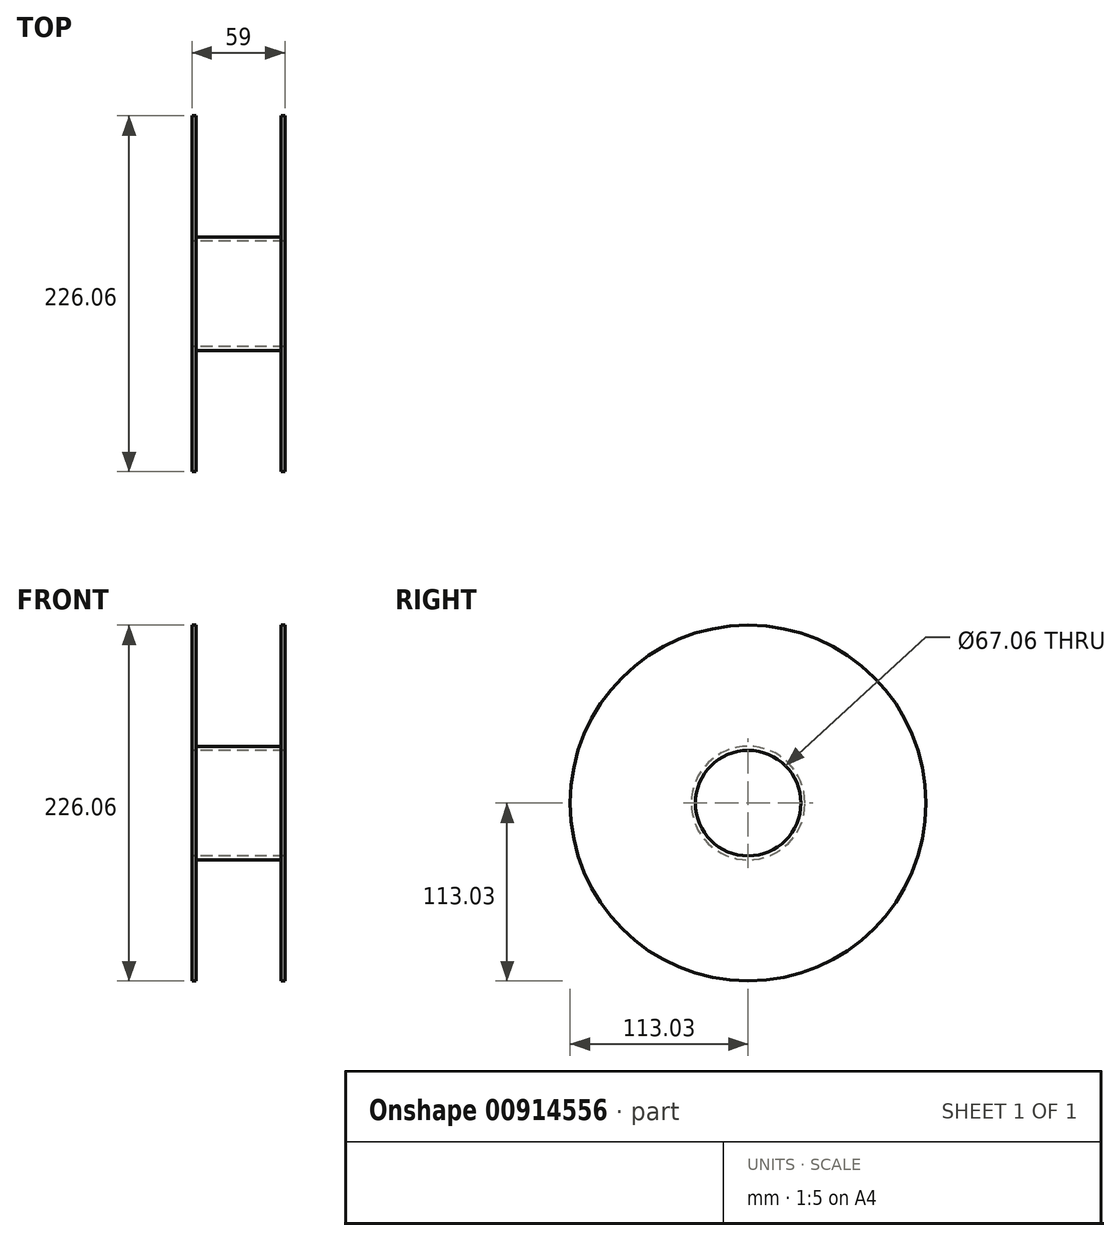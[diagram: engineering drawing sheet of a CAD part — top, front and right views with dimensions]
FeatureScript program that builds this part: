
annotation { "Feature Type Name" : "Feature", "Feature Type Description" : "" }
export const myFeature = defineFeature(function(context is Context, id is Id, definition is map)
    precondition{}
    {
        {
            var Q0;
            Q0=qCreatedBy(makeId("Front.planeOp"),FACE);
            var sketch = newSketch(context, id + "F0", { "sketchPlane" : qUnion([Q0])});
            skLineSegment(sketch, "E0", {"start": v(0, 0) * mm, "end": v(0, 33.53) * mm, "construction": true});
            skLineSegment(sketch, "E1", {"start": v(0, 33.53) * mm, "end": v(29.5, 33.53) * mm});
            skLineSegment(sketch, "E2.0", {"start": v(0, 36.07) * mm, "end": v(29.5, 36.07) * mm});
            skLineSegment(sketch, "E3", {"start": v(29.5, 33.53) * mm, "end": v(29.5, 113.03) * mm});
            skLineSegment(sketch, "E4.0", {"start": v(26.96, 33.53) * mm, "end": v(26.96, 113.03) * mm});
            skLineSegment(sketch, "E5", {"start": v(26.96, 113.03) * mm, "end": v(29.5, 113.03) * mm});
            skLineSegment(sketch, "E6.MirrorCS", {"start": v(-26.96, 113.03) * mm, "end": v(-29.5, 113.03) * mm});
            skLineSegment(sketch, "E7.MirrorCS", {"start": v(-29.5, 33.53) * mm, "end": v(-29.5, 113.03) * mm});
            skLineSegment(sketch, "E8.MirrorCS", {"start": v(-26.96, 33.53) * mm, "end": v(-26.96, 113.03) * mm});
            skLineSegment(sketch, "E9.MirrorCS", {"start": v(0, 36.07) * mm, "end": v(-29.5, 36.07) * mm});
            skLineSegment(sketch, "E10.MirrorCS", {"start": v(0, 33.53) * mm, "end": v(-29.5, 33.53) * mm});
            skLineSegment(sketch, "E11", {"start": v(0, 0) * mm, "end": v(27.71, 0) * mm, "construction": true});
            skSolve(sketch);
        }
        {
            var Q0;
            Q0 = qSketchRegion(id + "F0", true);
            var Q1;
            Q1=sQuery(id+"F0.wireOp",EDGE,"E11");
            revolve(context, id + "F1", {"surfaceOperationType" : NewSurfaceOperationType.NEW, "entities" : qUnion([Q0]), "axis" : qUnion([Q1]), "revolveType" : RevolveType.FULL});
        }
    });
